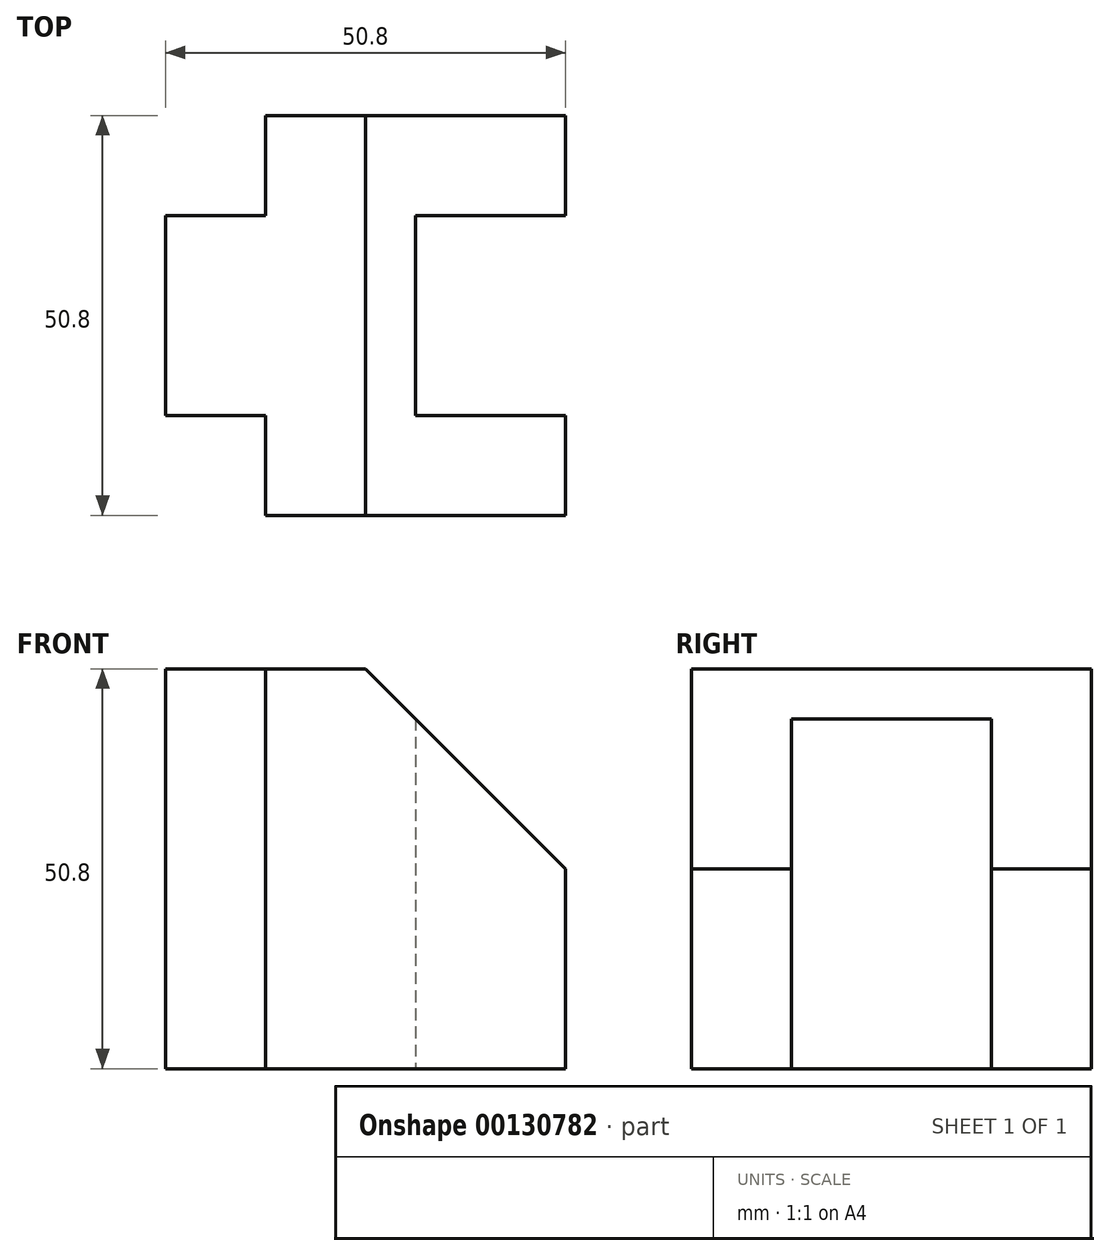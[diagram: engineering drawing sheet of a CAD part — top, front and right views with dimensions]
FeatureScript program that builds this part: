
annotation { "Feature Type Name" : "Feature", "Feature Type Description" : "" }
export const myFeature = defineFeature(function(context is Context, id is Id, definition is map)
    precondition{}
    {
        {
            var Q0;
            Q0=qCreatedBy(makeId("Front.planeOp"),FACE);
            var sketch = newSketch(context, id + "F0", { "sketchPlane" : qUnion([Q0])});
            skLineSegment(sketch, "E0.bottom", {"start": v(0, 0) * mm, "end": v(50.8, 0) * mm});
            skLineSegment(sketch, "E0.top", {"start": v(0, 50.8) * mm, "end": v(25.4, 50.8) * mm});
            skLineSegment(sketch, "E0.left", {"start": v(0, 0) * mm, "end": v(0, 50.8) * mm});
            skLineSegment(sketch, "E0.right", {"start": v(50.8, 0) * mm, "end": v(50.8, 25.4) * mm});
            skLineSegment(sketch, "E1", {"start": v(25.4, 50.8) * mm, "end": v(50.8, 25.4) * mm});
            skPoint(sketch, "E2.orphan", {"position": v(50.8, 50.8) * mm});
            skSolve(sketch);
        }
        {
            var Q0;
            Q0 = qSketchRegion(id + "F0", true);
            extrude(context, id + "F1", {"entities" : qUnion([Q0]), "depth" : 50.8 * mm});
        }
        {
            var Q0;
            Q0=makeQuery(id+"F1.opExtrude","SWEPT_FACE",FACE,{"disambiguationData":[OSD([sQuery(id+"F0.wireOp",EDGE,"E0.bottom")])]});
            var sketch = newSketch(context, id + "F2", { "sketchPlane" : qUnion([Q0])});
            skLineSegment(sketch, "E3", {"start": v(0, 38.1) * mm, "end": v(12.7, 38.1) * mm});
            skLineSegment(sketch, "E4", {"start": v(12.7, 38.1) * mm, "end": v(12.7, 50.8) * mm});
            skLineSegment(sketch, "E5", {"start": v(0, 12.7) * mm, "end": v(12.7, 12.7) * mm});
            skLineSegment(sketch, "E6", {"start": v(12.7, 12.7) * mm, "end": v(12.7, 0) * mm});
            skLineSegment(sketch, "E7", {"start": v(50.8, 38.1) * mm, "end": v(31.75, 38.1) * mm});
            skLineSegment(sketch, "E8", {"start": v(31.75, 38.1) * mm, "end": v(31.75, 12.7) * mm});
            skLineSegment(sketch, "E9", {"start": v(31.75, 12.7) * mm, "end": v(50.8, 12.7) * mm});
            skSolve(sketch);
        }
        {
            var Q0;
            {var subQ0=sQuery(id+"F2.wireOp",EDGE,"E3");Q0=makeQuery(id+"F2.imprint","IMPRINT",FACE,{"disambiguationData":[TD([[makeQuery(id+"F2.imprint","IMPRINT",EDGE,{"derivedFrom":subQ0}),1.0]])]});}
            var Q1;
            {var subQ0=sQuery(id+"F2.wireOp",EDGE,"E5");Q1=makeQuery(id+"F2.imprint","IMPRINT",FACE,{"disambiguationData":[TD([[makeQuery(id+"F2.imprint","IMPRINT",EDGE,{"derivedFrom":subQ0}),-1.0]])]});}
            extrude(context, id + "F3", {"entities" : qUnion([Q0, Q1]), "operationType" : NewBodyOperationType.REMOVE, "oppositeDirection" : true, "depth" : 50.8 * mm});
        }
        {
            var Q0;
            {var subQ0=sQuery(id+"F2.wireOp",EDGE,"E7");Q0=makeQuery(id+"F2.imprint","IMPRINT",FACE,{"disambiguationData":[TD([[makeQuery(id+"F2.imprint","IMPRINT",EDGE,{"derivedFrom":subQ0}),1.0]])]});}
            extrude(context, id + "F4", {"entities" : qUnion([Q0]), "operationType" : NewBodyOperationType.REMOVE, "endBound" : BoundingType.THROUGH_ALL, "oppositeDirection" : true, "depth" : 25.4 * mm});
        }
    });
